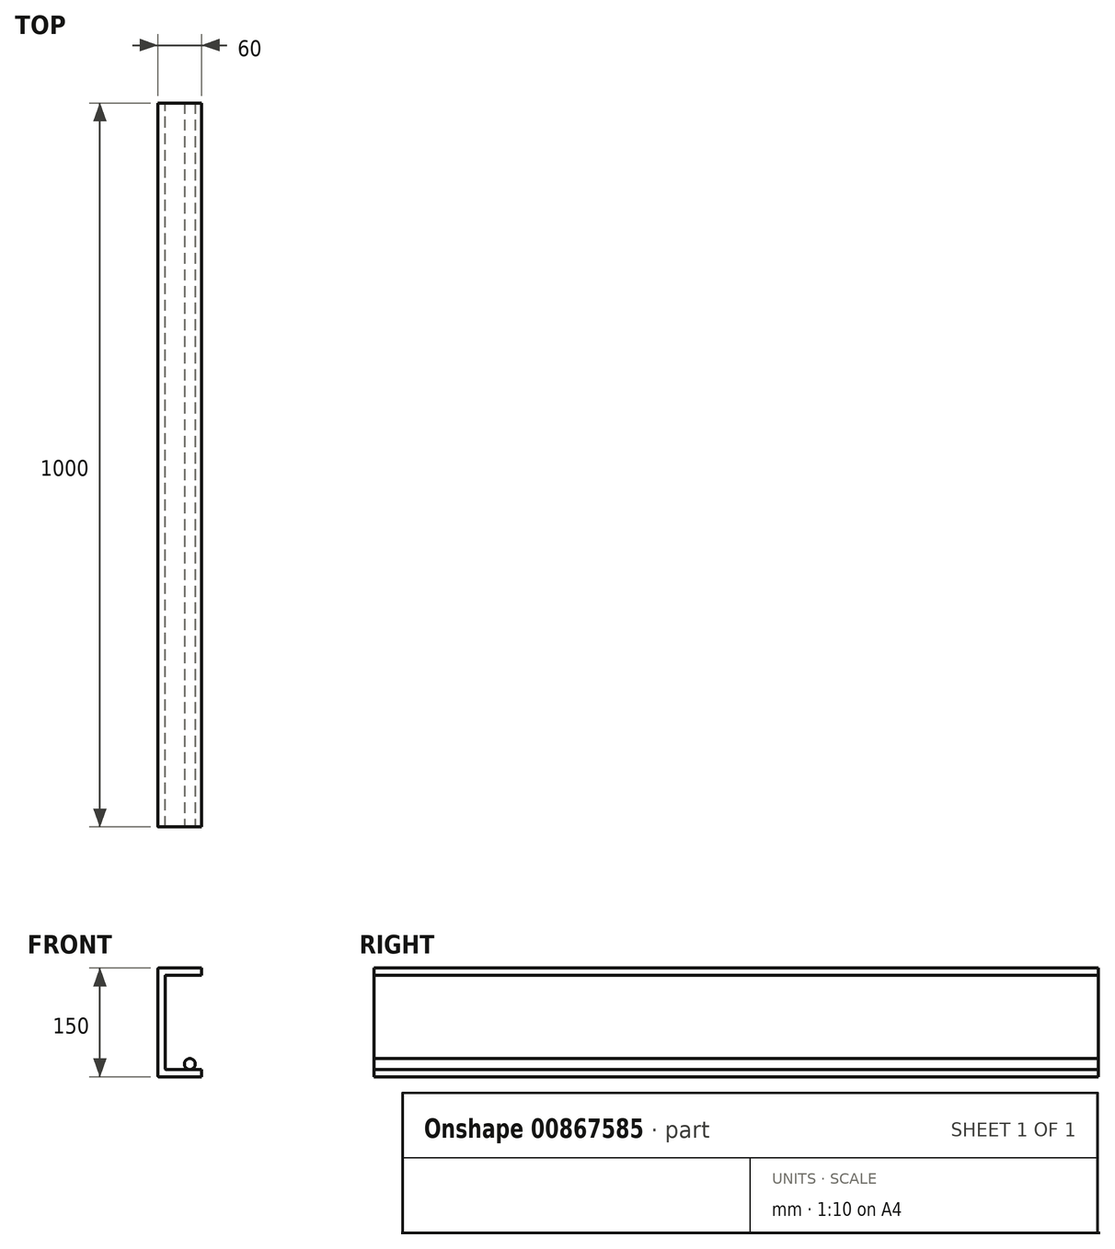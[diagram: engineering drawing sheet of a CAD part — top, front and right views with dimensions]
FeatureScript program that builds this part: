
annotation { "Feature Type Name" : "Feature", "Feature Type Description" : "" }
export const myFeature = defineFeature(function(context is Context, id is Id, definition is map)
    precondition{}
    {
        {
            var Q0;
            Q0=qCreatedBy(makeId("Front.planeOp"),FACE);
            var sketch = newSketch(context, id + "F0", { "sketchPlane" : qUnion([Q0])});
            skLineSegment(sketch, "E0", {"start": v(0, 1) * mm, "end": v(0, 149) * mm});
            skLineSegment(sketch, "E1", {"start": v(1, 150) * mm, "end": v(60, 150) * mm});
            skLineSegment(sketch, "E2", {"start": v(60, 150) * mm, "end": v(60, 140) * mm});
            skLineSegment(sketch, "E3", {"start": v(60, 140) * mm, "end": v(11, 140) * mm});
            skLineSegment(sketch, "E4", {"start": v(10, 139) * mm, "end": v(10, 11) * mm});
            skLineSegment(sketch, "E5", {"start": v(11, 10) * mm, "end": v(60, 10) * mm});
            skLineSegment(sketch, "E6", {"start": v(60, 10) * mm, "end": v(60, 0) * mm});
            skLineSegment(sketch, "E7", {"start": v(60, 0) * mm, "end": v(1, 0) * mm});
            skPoint(sketch, "E8.visualSharp", {"position": v(0, 150) * mm});
            skArc(sketch, "E8.filletArc", {"start": v(1, 150) * mm, "mid": v(0.3, 149.7) * mm, "end": v(0, 149) * mm});
            skPoint(sketch, "E9.visualSharp", {"position": v(10, 140) * mm});
            skArc(sketch, "E9.filletArc", {"start": v(11, 140) * mm, "mid": v(10.3, 139.7) * mm, "end": v(10, 139) * mm});
            skPoint(sketch, "E10.visualSharp", {"position": v(10, 10) * mm});
            skArc(sketch, "E10.filletArc", {"start": v(10, 11) * mm, "mid": v(10.3, 10.3) * mm, "end": v(11, 10) * mm});
            skPoint(sketch, "E11.visualSharp", {"position": v(0, 0) * mm});
            skArc(sketch, "E11.filletArc", {"start": v(0, 1) * mm, "mid": v(0.3, 0.3) * mm, "end": v(1, 0) * mm});
            skSolve(sketch);
        }
        {
            var Q0;
            Q0 = qSketchRegion(id + "F0", true);
            extrude(context, id + "F1", {"entities" : qUnion([Q0]), "endBound" : BoundingType.SYMMETRIC, "depth" : 1000 * mm, "offsetDistance" : 25 * mm});
        }
        {
            var Q0;
            Q0=makeQuery(id+"F1.opExtrude","CAP_FACE",FACE,{"disambiguationData":[OSD([sQuery(id+"F0.wireOp",EDGE,"E0"),sQuery(id+"F0.wireOp",EDGE,"E1"),sQuery(id+"F0.wireOp",EDGE,"E2"),sQuery(id+"F0.wireOp",EDGE,"E3"),sQuery(id+"F0.wireOp",EDGE,"E4"),sQuery(id+"F0.wireOp",EDGE,"E5"),sQuery(id+"F0.wireOp",EDGE,"E6"),sQuery(id+"F0.wireOp",EDGE,"E7")])],"isStart":false});
            var sketch = newSketch(context, id + "F2", { "sketchPlane" : qUnion([Q0])});
            skCircle(sketch, "E12", {"center": v(44.13, 17.5) * mm, "radius": 7.5 * mm});
            skSolve(sketch);
        }
        {
            var Q0;
            Q0 = qSketchRegion(id + "F2", true);
            extrude(context, id + "F3", {"entities" : qUnion([Q0]), "oppositeDirection" : true, "depth" : 1000 * mm, "offsetDistance" : 25 * mm});
        }
    });
